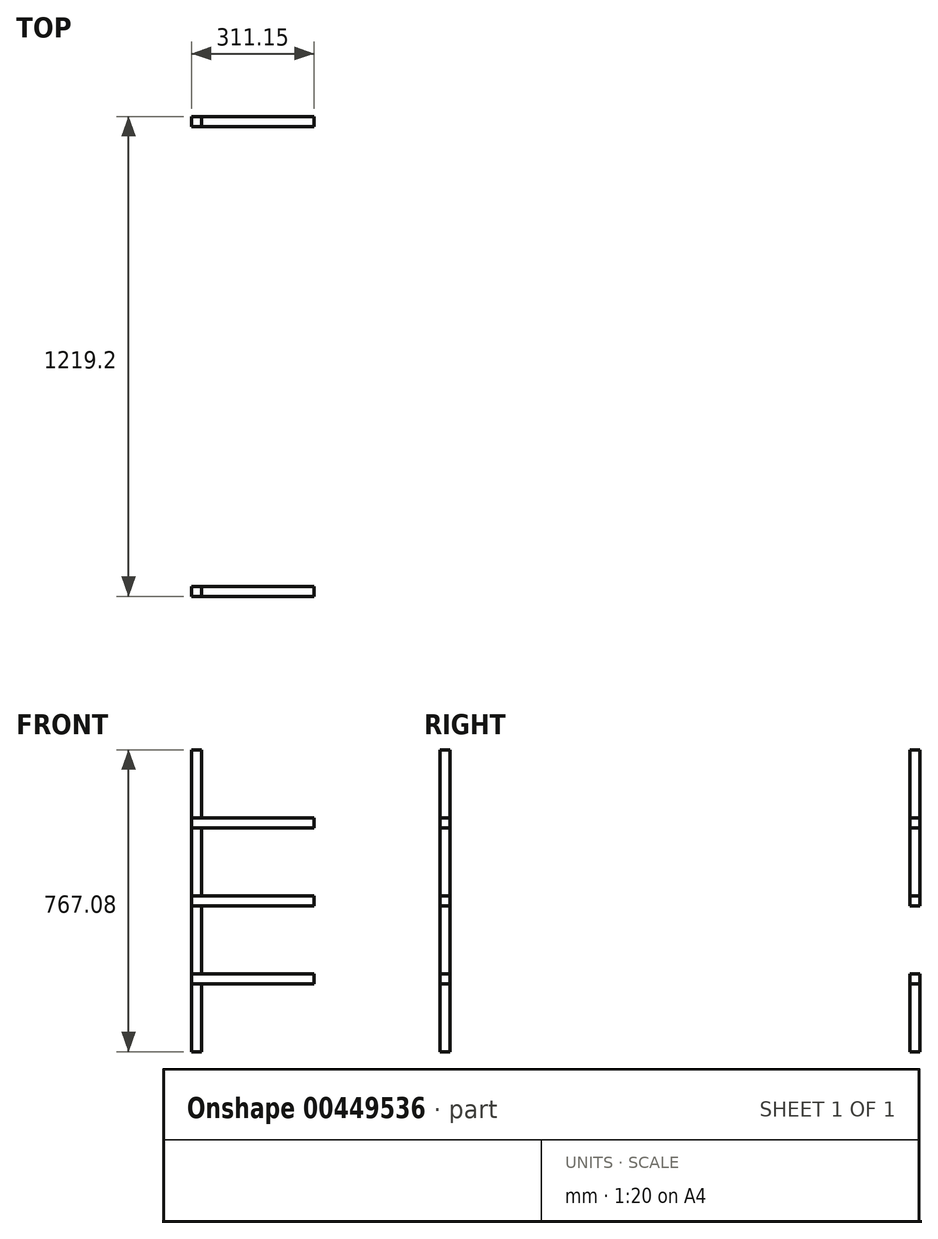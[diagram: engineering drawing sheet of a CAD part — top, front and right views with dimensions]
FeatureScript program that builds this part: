
annotation { "Feature Type Name" : "Feature", "Feature Type Description" : "" }
export const myFeature = defineFeature(function(context is Context, id is Id, definition is map)
    precondition{}
    {
        {
            var Q0;
            Q0=qCreatedBy(makeId("Right.planeOp"),FACE);
            var sketch = newSketch(context, id + "F0", { "sketchPlane" : qUnion([Q0])});
            skLineSegment(sketch, "E0.bottom", {"start": v(-1712.95, 815.95) * mm, "end": v(3950.23, 815.95) * mm});
            skLineSegment(sketch, "E0.top", {"start": v(-1712.95, -1927.25) * mm, "end": v(3950.23, -1927.25) * mm});
            skLineSegment(sketch, "E0.left", {"start": v(-1712.95, 815.95) * mm, "end": v(-1712.95, -1927.25) * mm});
            skLineSegment(sketch, "E0.right", {"start": v(3950.23, 815.95) * mm, "end": v(3950.23, -1927.25) * mm});
            skLineSegment(sketch, "E1", {"start": v(1118.64, 815.95) * mm, "end": v(1118.64, -1927.25) * mm});
            skLineSegment(sketch, "E2", {"start": v(-1712.95, 166.2) * mm, "end": v(1944.65, 166.2) * mm, "construction": true});
            skLineSegment(sketch, "E3", {"start": v(-1712.95, 511.15) * mm, "end": v(1335.05, 511.15) * mm, "construction": true});
            skLineSegment(sketch, "E4", {"start": v(-566.81, -1927.25) * mm, "end": v(-566.81, -631.85) * mm, "construction": true});
            skLineSegment(sketch, "E5", {"start": v(1118.64, 655.26) * mm, "end": v(-1742.01, 655.26) * mm});
            skLineSegment(sketch, "E6", {"start": v(-432.04, 815.95) * mm, "end": v(-432.04, 511.15) * mm, "construction": true});
            skLineSegment(sketch, "E7", {"start": v(406.74, -530.25) * mm, "end": v(406.74, 511.15) * mm});
            skLineSegment(sketch, "E8", {"start": v(-812.46, -479.45) * mm, "end": v(-812.46, 511.15) * mm});
            skLineSegment(sketch, "E9", {"start": v(406.74, -281.33) * mm, "end": v(-812.46, -281.33) * mm});
            skLineSegment(sketch, "E10", {"start": v(406.74, -83.2) * mm, "end": v(-812.46, -83.2) * mm});
            skLineSegment(sketch, "E11", {"start": v(406.74, 114.91) * mm, "end": v(-812.46, 114.91) * mm});
            skLineSegment(sketch, "E12", {"start": v(406.74, 313.03) * mm, "end": v(-812.46, 313.03) * mm});
            skLineSegment(sketch, "E13.left", {"start": v(406.74, 511.15) * mm, "end": v(406.74, -479.45) * mm});
            skText(sketch, "E14", { "text": "use tape for wall marking instead of pencil marks!", "fontName": "OpenSans-Regular.ttf"});
            skLineSegment(sketch, "E15.bottom", {"start": v(-812.46, -281.33) * mm, "end": v(-787.06, -281.33) * mm});
            skLineSegment(sketch, "E15.top", {"start": v(-812.46, -255.93) * mm, "end": v(-787.06, -255.93) * mm});
            skLineSegment(sketch, "E15.left", {"start": v(-812.46, -281.33) * mm, "end": v(-812.46, -255.93) * mm});
            skLineSegment(sketch, "E15.right", {"start": v(-787.06, -281.33) * mm, "end": v(-787.06, -255.93) * mm});
            skLineSegment(sketch, "E16.bottom", {"start": v(406.74, -281.33) * mm, "end": v(381.84, -281.33) * mm});
            skLineSegment(sketch, "E16.left", {"start": v(406.74, -525.34) * mm, "end": v(406.74, -281.33) * mm});
            skLineSegment(sketch, "E17.top", {"start": v(393.44, -83.2) * mm, "end": v(406.74, -83.2) * mm});
            skLineSegment(sketch, "E18.bottom", {"start": v(381.34, 140.31) * mm, "end": v(406.74, 140.31) * mm});
            skLineSegment(sketch, "E18.top", {"start": v(381.34, 114.91) * mm, "end": v(406.74, 114.91) * mm});
            skLineSegment(sketch, "E18.left", {"start": v(381.34, 140.31) * mm, "end": v(381.34, 114.91) * mm});
            skLineSegment(sketch, "E18.right", {"start": v(406.74, 140.31) * mm, "end": v(406.74, 114.91) * mm});
            skLineSegment(sketch, "E19.top", {"start": v(395.5, 313.03) * mm, "end": v(406.74, 313.03) * mm});
            skLineSegment(sketch, "E19.right", {"start": v(406.74, 313.03) * mm, "end": v(406.74, 100.43) * mm});
            skLineSegment(sketch, "E20.bottom", {"start": v(-787.06, -57.8) * mm, "end": v(-812.46, -57.8) * mm});
            skLineSegment(sketch, "E20.top", {"start": v(-787.06, -83.2) * mm, "end": v(-812.46, -83.2) * mm});
            skLineSegment(sketch, "E20.left", {"start": v(-787.06, -57.8) * mm, "end": v(-787.06, -83.2) * mm});
            skLineSegment(sketch, "E20.right", {"start": v(-812.46, -57.8) * mm, "end": v(-812.46, -83.2) * mm});
            skLineSegment(sketch, "E21.bottom", {"start": v(-787.06, 140.31) * mm, "end": v(-812.46, 140.31) * mm});
            skLineSegment(sketch, "E21.top", {"start": v(-787.06, 114.91) * mm, "end": v(-812.46, 114.91) * mm});
            skLineSegment(sketch, "E21.left", {"start": v(-787.06, 140.31) * mm, "end": v(-787.06, 114.91) * mm});
            skLineSegment(sketch, "E21.right", {"start": v(-812.46, 140.31) * mm, "end": v(-812.46, 114.91) * mm});
            skLineSegment(sketch, "E22.bottom", {"start": v(-787.06, 338.43) * mm, "end": v(-812.46, 338.43) * mm});
            skLineSegment(sketch, "E22.top", {"start": v(-787.06, 313.03) * mm, "end": v(-812.46, 313.03) * mm});
            skLineSegment(sketch, "E22.left", {"start": v(-787.06, 338.43) * mm, "end": v(-787.06, 313.03) * mm});
            skLineSegment(sketch, "E22.right", {"start": v(-812.46, 338.43) * mm, "end": v(-812.46, 313.03) * mm});
            skLineSegment(sketch, "E23.bottom", {"start": v(406.74, -57.8) * mm, "end": v(381.34, -57.8) * mm});
            skLineSegment(sketch, "E23.top", {"start": v(406.74, -83.2) * mm, "end": v(381.34, -83.2) * mm});
            skLineSegment(sketch, "E23.left", {"start": v(406.74, -57.8) * mm, "end": v(406.74, -83.2) * mm});
            skLineSegment(sketch, "E23.right", {"start": v(381.34, -57.8) * mm, "end": v(381.34, -83.2) * mm});
            skPoint(sketch, "E23.middle", {"position": v(394.04, -70.5) * mm});
            skLineSegment(sketch, "E24", {"start": v(406.74, -479.45) * mm, "end": v(-812.46, -479.45) * mm});
            skLineSegment(sketch, "E25", {"start": v(-812.46, 511.15) * mm, "end": v(406.74, 511.15) * mm});
            skLineSegment(sketch, "E26", {"start": v(-812.46, -479.45) * mm, "end": v(406.74, -479.45) * mm});
            skLineSegment(sketch, "E27.bottom", {"start": v(-812.46, -479.45) * mm, "end": v(-787.06, -479.45) * mm});
            skLineSegment(sketch, "E27.top", {"start": v(-812.46, 511.15) * mm, "end": v(-787.06, 511.15) * mm});
            skLineSegment(sketch, "E27.right", {"start": v(-787.06, -479.45) * mm, "end": v(-787.06, 511.15) * mm});
            skLineSegment(sketch, "E28.bottom", {"start": v(406.74, -479.45) * mm, "end": v(381.34, -479.45) * mm});
            skLineSegment(sketch, "E28.top", {"start": v(406.74, 511.15) * mm, "end": v(381.34, 511.15) * mm});
            skLineSegment(sketch, "E28.left", {"start": v(406.74, -479.45) * mm, "end": v(406.74, 511.15) * mm});
            skLineSegment(sketch, "E28.right", {"start": v(381.34, -479.45) * mm, "end": v(381.34, 511.15) * mm});
            skLineSegment(sketch, "E29.left", {"start": v(-812.46, -479.45) * mm, "end": v(-812.46, -296.33) * mm});
            skLineSegment(sketch, "E29.right", {"start": v(-787.06, -479.45) * mm, "end": v(-787.06, -296.33) * mm});
            skLineSegment(sketch, "E30.bottom", {"start": v(381.34, -479.45) * mm, "end": v(406.74, -479.45) * mm});
            skLineSegment(sketch, "E30.top", {"start": v(381.34, -454.05) * mm, "end": v(406.74, -454.05) * mm});
            skLineSegment(sketch, "E30.left", {"start": v(381.34, -479.45) * mm, "end": v(381.34, -454.05) * mm});
            skLineSegment(sketch, "E30.right", {"start": v(406.74, -479.45) * mm, "end": v(406.74, -454.05) * mm});
            skLineSegment(sketch, "E31.bottom", {"start": v(381.34, -255.93) * mm, "end": v(406.74, -255.93) * mm});
            skLineSegment(sketch, "E31.left", {"start": v(381.34, -454.05) * mm, "end": v(381.34, -255.93) * mm});
            skLineSegment(sketch, "E31.right", {"start": v(406.74, -454.05) * mm, "end": v(406.74, -255.93) * mm});
            skLineSegment(sketch, "E32.bottom", {"start": v(381.34, 313.03) * mm, "end": v(406.74, 313.03) * mm});
            skLineSegment(sketch, "E32.top", {"start": v(381.34, 338.43) * mm, "end": v(406.74, 338.43) * mm});
            skLineSegment(sketch, "E32.left", {"start": v(381.34, 313.03) * mm, "end": v(381.34, 338.43) * mm});
            skLineSegment(sketch, "E32.right", {"start": v(406.74, 313.03) * mm, "end": v(406.74, 338.43) * mm});
            skLineSegment(sketch, "E33.top", {"start": v(-812.46, -454.05) * mm, "end": v(-787.06, -454.05) * mm});
            skLineSegment(sketch, "E33.left", {"start": v(-812.46, -479.45) * mm, "end": v(-812.46, -454.05) * mm});
            skLineSegment(sketch, "E33.right", {"start": v(-787.06, -479.45) * mm, "end": v(-787.06, -454.05) * mm});
            skLineSegment(sketch, "E34.bottom", {"start": v(381.34, 511.15) * mm, "end": v(406.74, 511.15) * mm});
            skLineSegment(sketch, "E34.top", {"start": v(381.34, 536.55) * mm, "end": v(406.74, 536.55) * mm});
            skLineSegment(sketch, "E34.left", {"start": v(381.34, 511.15) * mm, "end": v(381.34, 536.55) * mm});
            skLineSegment(sketch, "E34.right", {"start": v(406.74, 511.15) * mm, "end": v(406.74, 536.55) * mm});
            skLineSegment(sketch, "E35.top", {"start": v(-812.46, 536.55) * mm, "end": v(-787.06, 536.55) * mm});
            skLineSegment(sketch, "E35.left", {"start": v(-812.46, 511.15) * mm, "end": v(-812.46, 536.55) * mm});
            skLineSegment(sketch, "E35.right", {"start": v(-787.06, 511.15) * mm, "end": v(-787.06, 536.55) * mm});
            const initialGuessF0  = {"E14": [-2.41378, 1.35413, 1, 0, 0.42184]};
            skSetInitialGuess(sketch, initialGuessF0);
            skSolve(sketch);
        }
        {
            var Q0;
            {var subQ0=sQuery(id+"F0.wireOp",EDGE,"E21.bottom");Q0=makeQuery(id+"F0.imprint","IMPRINT",FACE,{"disambiguationData":[TD([[makeQuery(id+"F0.imprint","IMPRINT",EDGE,{"derivedFrom":subQ0}),1.0]])]});}
            var Q1;
            Q1=makeQuery(id+"F0.imprint","IMPRINT",FACE,{"disambiguationData":[TD([[makeQuery(id+"F0.imprint","IMPRINT",EDGE,{"derivedFrom":sQuery(id+"F0.wireOp",EDGE,"E27.bottom")}),1.0]])]});
            var Q2;
            {var subQ0=sQuery(id+"F0.wireOp",EDGE,"E22.bottom");Q2=makeQuery(id+"F0.imprint","IMPRINT",FACE,{"disambiguationData":[TD([[makeQuery(id+"F0.imprint","IMPRINT",EDGE,{"derivedFrom":subQ0}),1.0]])]});}
            var Q3;
            {var subQ0=sQuery(id+"F0.wireOp",EDGE,"E15.bottom");Q3=makeQuery(id+"F0.imprint","IMPRINT",FACE,{"disambiguationData":[TD([[makeQuery(id+"F0.imprint","IMPRINT",EDGE,{"derivedFrom":subQ0}),1.0]])]});}
            var Q4;
            {var subQ0=sQuery(id+"F0.wireOp",EDGE,"E20.bottom");Q4=makeQuery(id+"F0.imprint","IMPRINT",FACE,{"disambiguationData":[TD([[makeQuery(id+"F0.imprint","IMPRINT",EDGE,{"derivedFrom":subQ0}),1.0]])]});}
            var Q5;
            Q5=makeQuery(id+"F0.imprint","IMPRINT",FACE,{"disambiguationData":[TD([[makeQuery(id+"F0.imprint","IMPRINT",EDGE,{"derivedFrom":sQuery(id+"F0.wireOp",EDGE,"E27.top")}),1.0]])]});
            extrude(context, id + "F1", {"entities" : qUnion([Q0, Q1, Q2, Q3, Q4, Q5]), "depth" : 311.15 * mm});
        }
        {
            var Q0;
            {var subQ0=sQuery(id+"F0.wireOp",EDGE,"E15.top");Q0=makeQuery(id+"F0.imprint","IMPRINT",FACE,{"disambiguationData":[TD([[makeQuery(id+"F0.imprint","IMPRINT",EDGE,{"derivedFrom":subQ0}),1.0]])]});}
            var Q1;
            {var subQ0=sQuery(id+"F0.wireOp",EDGE,"E21.bottom");Q1=makeQuery(id+"F0.imprint","IMPRINT",FACE,{"disambiguationData":[TD([[makeQuery(id+"F0.imprint","IMPRINT",EDGE,{"derivedFrom":subQ0}),-1.0]])]});}
            var Q2;
            {var subQ0=sQuery(id+"F0.wireOp",EDGE,"E22.bottom");Q2=makeQuery(id+"F0.imprint","IMPRINT",FACE,{"disambiguationData":[TD([[makeQuery(id+"F0.imprint","IMPRINT",EDGE,{"derivedFrom":subQ0}),-1.0]])]});}
            var Q3;
            {var subQ0=sQuery(id+"F0.wireOp",EDGE,"E20.bottom");Q3=makeQuery(id+"F0.imprint","IMPRINT",FACE,{"disambiguationData":[TD([[makeQuery(id+"F0.imprint","IMPRINT",EDGE,{"derivedFrom":subQ0}),-1.0]])]});}
            var Q4;
            {var subQ2=sQuery(id+"F0.wireOp",EDGE,"E15.bottom");Q4=makeQuery(id+"F0.imprint","IMPRINT",FACE,{"disambiguationData":[TD([[makeQuery(id+"F0.imprint","IMPRINT",EDGE,{"derivedFrom":subQ2}),-1.0]])]});}
            extrude(context, id + "F2", {"entities" : qUnion([Q0, Q1, Q2, Q3, Q4]), "depth" : 25.4 * mm});
        }
        {
            var Q0;
            {var subQ1=sQuery(id+"F0.wireOp",EDGE,"E18.top");Q0=makeQuery(id+"F0.imprint","IMPRINT",FACE,{"disambiguationData":[TD([[makeQuery(id+"F0.imprint","IMPRINT",EDGE,{"derivedFrom":subQ1}),-1.0]])]});}
            var Q1;
            {var subQ3=sQuery(id+"F0.wireOp",EDGE,"E31.bottom");Q1=makeQuery(id+"F0.imprint","IMPRINT",FACE,{"disambiguationData":[TD([[makeQuery(id+"F0.imprint","IMPRINT",EDGE,{"derivedFrom":subQ3}),1.0]])]});}
            var Q2;
            {var subQ2=sQuery(id+"F0.wireOp",EDGE,"E32.top");Q2=makeQuery(id+"F0.imprint","IMPRINT",FACE,{"disambiguationData":[TD([[makeQuery(id+"F0.imprint","IMPRINT",EDGE,{"derivedFrom":subQ2}),1.0]])]});}
            var Q3;
            {var subQ4=sQuery(id+"F0.wireOp",EDGE,"E16.bottom");Q3=makeQuery(id+"F0.imprint","IMPRINT",FACE,{"disambiguationData":[TD([[makeQuery(id+"F0.imprint","IMPRINT",EDGE,{"derivedFrom":subQ4}),1.0]])]});}
            var Q4;
            {var subQ3=sQuery(id+"F0.wireOp",EDGE,"E18.bottom");Q4=makeQuery(id+"F0.imprint","IMPRINT",FACE,{"disambiguationData":[TD([[makeQuery(id+"F0.imprint","IMPRINT",EDGE,{"derivedFrom":subQ3}),1.0]])]});}
            extrude(context, id + "F3", {"entities" : qUnion([Q0, Q1, Q2, Q3, Q4]), "depth" : 25.4 * mm});
        }
        {
            var Q0;
            Q0=makeQuery(id+"F0.imprint","IMPRINT",FACE,{"disambiguationData":[TD([[makeQuery(id+"F0.imprint","IMPRINT",EDGE,{"derivedFrom":sQuery(id+"F0.wireOp",EDGE,"E32.top")}),-1.0]])]});
            var Q1;
            Q1=makeQuery(id+"F0.imprint","IMPRINT",FACE,{"disambiguationData":[TD([[makeQuery(id+"F0.imprint","IMPRINT",EDGE,{"derivedFrom":sQuery(id+"F0.wireOp",EDGE,"E34.bottom")}),1.0]])]});
            var Q2;
            Q2=makeQuery(id+"F0.imprint","IMPRINT",FACE,{"disambiguationData":[TD([[makeQuery(id+"F0.imprint","IMPRINT",EDGE,{"derivedFrom":sQuery(id+"F0.wireOp",EDGE,"E30.bottom")}),1.0]])]});
            var Q3;
            {var subQ1=sQuery(id+"F0.wireOp",EDGE,"E16.bottom");Q3=makeQuery(id+"F0.imprint","IMPRINT",FACE,{"disambiguationData":[TD([[makeQuery(id+"F0.imprint","IMPRINT",EDGE,{"derivedFrom":subQ1}),-1.0]])]});}
            var Q4;
            {var subQ0=sQuery(id+"F0.wireOp",EDGE,"E18.bottom");Q4=makeQuery(id+"F0.imprint","IMPRINT",FACE,{"disambiguationData":[TD([[makeQuery(id+"F0.imprint","IMPRINT",EDGE,{"derivedFrom":subQ0}),-1.0]])]});}
            var Q5;
            {var subQ1=sQuery(id+"F0.wireOp",EDGE,"E23.bottom");Q5=makeQuery(id+"F0.imprint","IMPRINT",FACE,{"disambiguationData":[TD([[makeQuery(id+"F0.imprint","IMPRINT",EDGE,{"derivedFrom":subQ1}),1.0]])]});}
            extrude(context, id + "F4", {"entities" : qUnion([Q0, Q1, Q2, Q3, Q4, Q5]), "depth" : 311.15 * mm});
        }
    });
